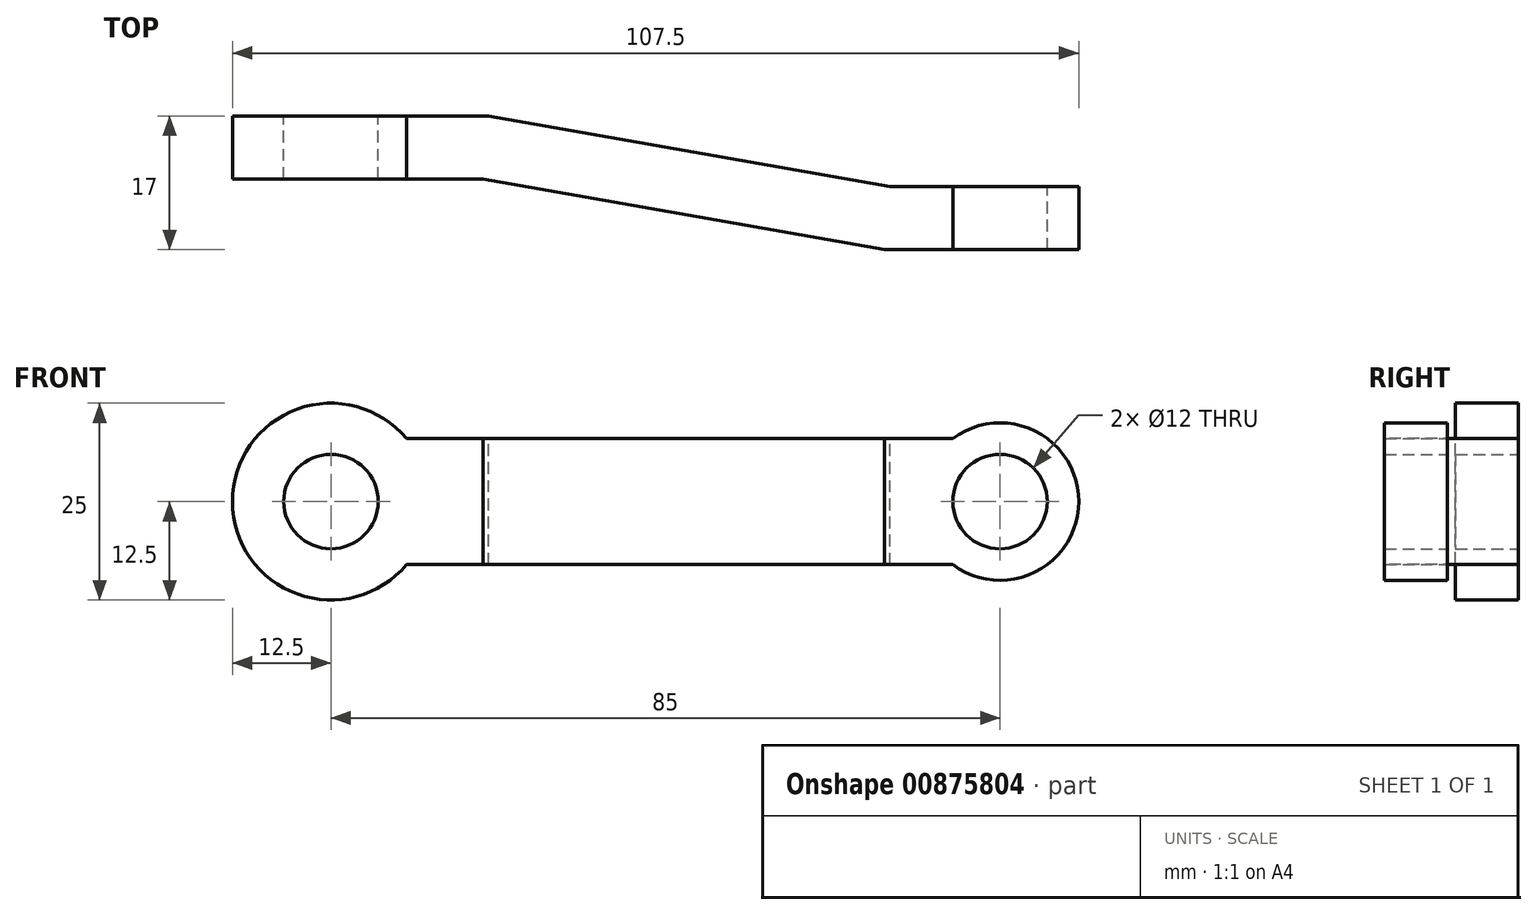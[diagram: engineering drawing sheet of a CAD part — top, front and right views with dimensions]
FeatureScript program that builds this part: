
annotation { "Feature Type Name" : "Feature", "Feature Type Description" : "" }
export const myFeature = defineFeature(function(context is Context, id is Id, definition is map)
    precondition{}
    {
        {
            var Q0;
            Q0=qCreatedBy(makeId("Front.planeOp"),FACE);
            var sketch = newSketch(context, id + "F0", { "sketchPlane" : qUnion([Q0])});
            skCircle(sketch, "E0", {"center": v(0, 0) * mm, "radius": 12.5 * mm});
            skCircle(sketch, "E1", {"center": v(85, 0) * mm, "radius": 10 * mm});
            skLineSegment(sketch, "E2", {"start": v(0, 0) * mm, "end": v(85, 0) * mm, "construction": true});
            skLineSegment(sketch, "E3", {"start": v(9.6, 8) * mm, "end": v(79, 8) * mm});
            skLineSegment(sketch, "E4.MirrorCS", {"start": v(9.6, -8) * mm, "end": v(79, -8) * mm});
            skCircle(sketch, "E5", {"center": v(0, 0) * mm, "radius": 6 * mm});
            skCircle(sketch, "E6", {"center": v(85, 0) * mm, "radius": 6 * mm});
            skSolve(sketch);
        }
        {
            var Q0;
            Q0 = qSketchRegion(id + "F0", true);
            extrude(context, id + "F1", {"entities" : qUnion([Q0]), "depth" : 25 * mm, "offsetDistance" : 25 * mm});
        }
        {
            var Q0;
            Q0=qCreatedBy(makeId("Top.planeOp"),FACE);
            var sketch = newSketch(context, id + "F2", { "sketchPlane" : qUnion([Q0])});
            skLineSegment(sketch, "E7", {"start": v(0, 0) * mm, "end": v(20, 0) * mm});
            skLineSegment(sketch, "E8", {"start": v(20, 0) * mm, "end": v(71.04, -9) * mm});
            skLineSegment(sketch, "E9", {"start": v(71.04, -9) * mm, "end": v(95, -9) * mm});
            skLineSegment(sketch, "E10", {"start": v(0, 0) * mm, "end": v(-12.5, 0) * mm});
            skLineSegment(sketch, "E11.0", {"start": v(70.34, -17) * mm, "end": v(95, -17) * mm});
            skLineSegment(sketch, "E11.1", {"start": v(19.3, -8) * mm, "end": v(70.34, -17) * mm});
            skLineSegment(sketch, "E11.2", {"start": v(0, -8) * mm, "end": v(19.3, -8) * mm});
            skLineSegment(sketch, "E11.3", {"start": v(0, -8) * mm, "end": v(-12.5, -8) * mm});
            skLineSegment(sketch, "E12", {"start": v(95, -17) * mm, "end": v(95, -9) * mm});
            skLineSegment(sketch, "E13", {"start": v(-12.5, -8) * mm, "end": v(-12.5, 0) * mm});
            skLineSegment(sketch, "E14", {"start": v(95, 0) * mm, "end": v(95, -25) * mm});
            skLineSegment(sketch, "E15", {"start": v(-12.5, -25) * mm, "end": v(-12.5, 0) * mm});
            skSolve(sketch);
        }
        {
            var Q0;
            Q0 = qSketchRegion(id + "F2", true);
            extrude(context, id + "F3", {"entities" : qUnion([Q0]), "operationType" : NewBodyOperationType.INTERSECT, "endBound" : BoundingType.SYMMETRIC, "oppositeDirection" : true, "depth" : 25 * mm, "offsetDistance" : 25 * mm});
        }
    });
